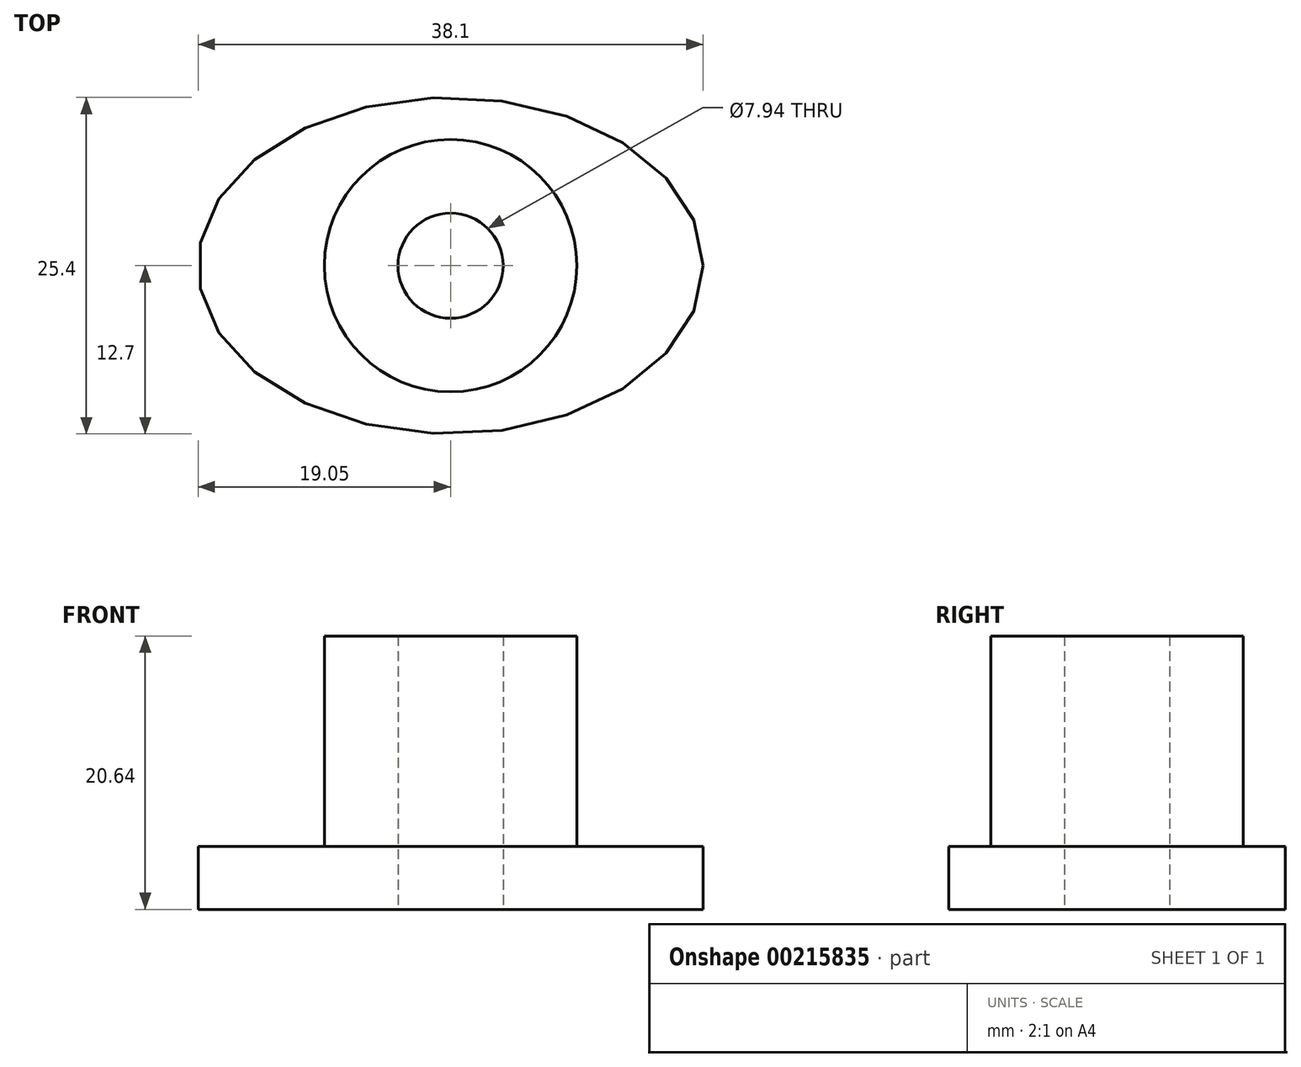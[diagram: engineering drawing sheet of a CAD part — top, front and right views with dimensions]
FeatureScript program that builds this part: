
annotation { "Feature Type Name" : "Feature", "Feature Type Description" : "" }
export const myFeature = defineFeature(function(context is Context, id is Id, definition is map)
    precondition{}
    {
        {
            var Q0;
            Q0=qCreatedBy(makeId("Top.planeOp"),FACE);
            var sketch = newSketch(context, id + "F0", { "sketchPlane" : qUnion([Q0])});
            skEllipse(sketch, "E0", {"center": v(0, 0) * mm, "majorRadius": 19.05 * mm, "minorRadius": 12.7 * mm, "majorAxis": v(1, 0)});
            skCircle(sketch, "E1", {"center": v(0, 0) * mm, "radius": 9.53 * mm});
            skCircle(sketch, "E2", {"center": v(0, 0) * mm, "radius": 3.97 * mm});
            skSolve(sketch);
        }
        {
            var Q0;
            Q0=makeQuery(id+"F0.imprint","IMPRINT",FACE,{"disambiguationData":[TD([[makeQuery(id+"F0.imprint","IMPRINT",EDGE,{"derivedFrom":sQuery(id+"F0.wireOp",EDGE,"E0")}),1.0]])]});
            var Q1;
            Q1=makeQuery(id+"F0.imprint","IMPRINT",FACE,{"disambiguationData":[TD([[makeQuery(id+"F0.imprint","IMPRINT",EDGE,{"derivedFrom":sQuery(id+"F0.wireOp",EDGE,"E1")}),1.0]])]});
            extrude(context, id + "F1", {"entities" : qUnion([Q0, Q1]), "depth" : 4.76 * mm});
        }
        {
            var Q0;
            Q0=makeQuery(id+"F0.imprint","IMPRINT",FACE,{"disambiguationData":[TD([[makeQuery(id+"F0.imprint","IMPRINT",EDGE,{"derivedFrom":sQuery(id+"F0.wireOp",EDGE,"E1")}),1.0]])]});
            extrude(context, id + "F2", {"entities" : qUnion([Q0]), "operationType" : NewBodyOperationType.ADD, "depth" : 20.64 * mm});
        }
    });
